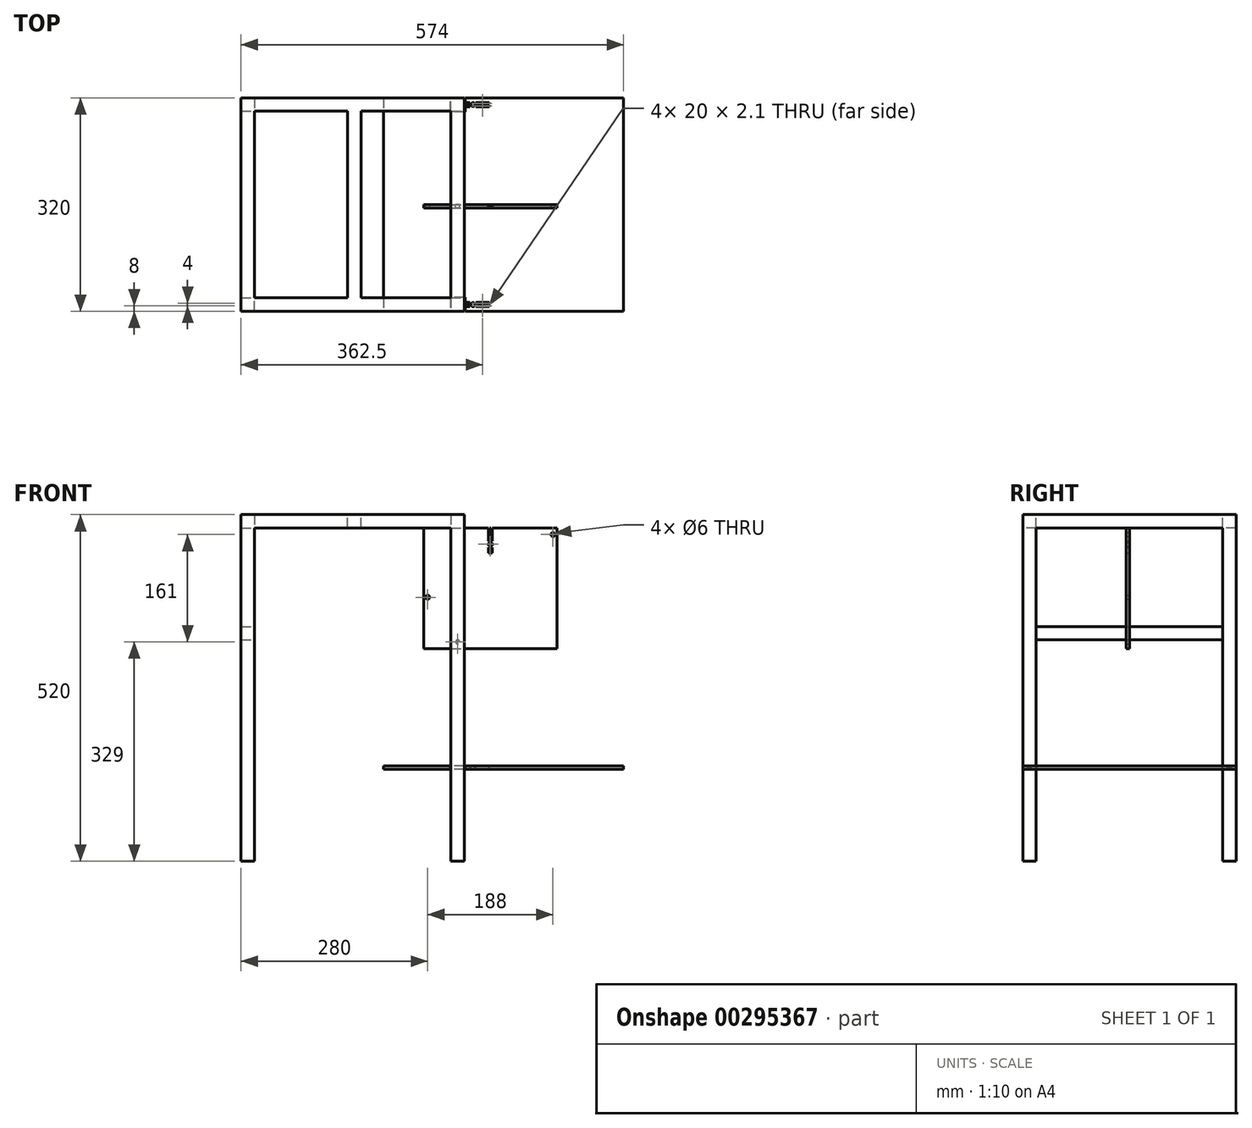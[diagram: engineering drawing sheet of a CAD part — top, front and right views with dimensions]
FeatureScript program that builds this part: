
annotation { "Feature Type Name" : "Feature", "Feature Type Description" : "" }
export const myFeature = defineFeature(function(context is Context, id is Id, definition is map)
    precondition{}
    {
        {
            var Q0;
            Q0=qCreatedBy(makeId("Front.planeOp"),FACE);
            var sketch = newSketch(context, id + "F0", { "sketchPlane" : qUnion([Q0])});
            skCircle(sketch, "E0", {"center": v(0, 0) * mm, "radius": 3 * mm});
            skCircle(sketch, "E1", {"center": v(-45, 67) * mm, "radius": 3 * mm});
            skCircle(sketch, "E2", {"center": v(143, 161) * mm, "radius": 3 * mm});
            skLineSegment(sketch, "E3.bottom", {"start": v(-51, -10) * mm, "end": v(149, -10) * mm});
            skLineSegment(sketch, "E3.top", {"start": v(-51, 171) * mm, "end": v(45.95, 171) * mm});
            skLineSegment(sketch, "E3.left", {"start": v(-51, -10) * mm, "end": v(-51, 171) * mm});
            skLineSegment(sketch, "E3.right", {"start": v(149, -10) * mm, "end": v(149, 171) * mm});
            skCircle(sketch, "E4", {"center": v(49, 146.5) * mm, "radius": 3 * mm});
            skPoint(sketch, "E4.centerSnap0", {"position": v(49, 171) * mm});
            skLineSegment(sketch, "E5.top", {"start": v(45.95, 151) * mm, "end": v(48.05, 151) * mm});
            skLineSegment(sketch, "E5.left", {"start": v(45.95, 171) * mm, "end": v(45.95, 151) * mm});
            skLineSegment(sketch, "E5.right", {"start": v(48.05, 171) * mm, "end": v(48.05, 151) * mm});
            skLineSegment(sketch, "E6.bottom", {"start": v(45.95, 141.5) * mm, "end": v(48.05, 141.5) * mm});
            skLineSegment(sketch, "E6.top", {"start": v(45.95, 133.5) * mm, "end": v(48.05, 133.5) * mm});
            skLineSegment(sketch, "E6.left", {"start": v(45.95, 141.5) * mm, "end": v(45.95, 133.5) * mm});
            skLineSegment(sketch, "E6.right", {"start": v(48.05, 141.5) * mm, "end": v(48.05, 133.5) * mm});
            skLineSegment(sketch, "E7.trimOffspring", {"start": v(48.05, 171) * mm, "end": v(49.95, 171) * mm});
            skLineSegment(sketch, "E8.MirrorCS", {"start": v(52.05, 133.5) * mm, "end": v(49.95, 133.5) * mm});
            skLineSegment(sketch, "E9.MirrorCS", {"start": v(52.05, 141.5) * mm, "end": v(49.95, 141.5) * mm});
            skLineSegment(sketch, "E10.MirrorCS", {"start": v(49.95, 171) * mm, "end": v(49.95, 151) * mm});
            skLineSegment(sketch, "E11.MirrorCS", {"start": v(52.05, 151) * mm, "end": v(49.95, 151) * mm});
            skLineSegment(sketch, "E12.MirrorCS", {"start": v(52.05, 141.5) * mm, "end": v(52.05, 133.5) * mm});
            skLineSegment(sketch, "E13.MirrorCS", {"start": v(49.95, 141.5) * mm, "end": v(49.95, 133.5) * mm});
            skLineSegment(sketch, "E14.MirrorCS", {"start": v(52.05, 171) * mm, "end": v(52.05, 151) * mm});
            skLineSegment(sketch, "E15.trimOffspring", {"start": v(52.05, 171) * mm, "end": v(149, 171) * mm});
            skSolve(sketch);
        }
        {
            var Q0;
            Q0=makeQuery(id+"F0.imprint","IMPRINT",FACE,{"disambiguationData":[TD([[makeQuery(id+"F0.imprint","IMPRINT",EDGE,{"derivedFrom":sQuery(id+"F0.wireOp",EDGE,"E0")}),-1.0]])]});
            extrude(context, id + "F1", {"entities" : qUnion([Q0]), "depth" : 5 * mm});
        }
        {
            var Q0;
            Q0=qCreatedBy(makeId("Top.planeOp"),FACE);
            cPlane(context, id + "F2", {"entities" : qUnion([Q0]), "cplaneType" : CPlaneType.OFFSET, "offset" : 171 * mm, "width" : 150 * mm, "height" : 150 * mm});
        }
        {
            var Q0;
            Q0=qCreatedBy(id+"F2.planeOp",FACE);
            var sketch = newSketch(context, id + "F3", { "sketchPlane" : qUnion([Q0])});
            skLineSegment(sketch, "E16.bottom", {"start": v(10, -160) * mm, "end": v(-10, -160) * mm});
            skLineSegment(sketch, "E16.top", {"start": v(10, 160) * mm, "end": v(-10, 160) * mm});
            skLineSegment(sketch, "E16.left", {"start": v(10, -160) * mm, "end": v(10, 160) * mm});
            skLineSegment(sketch, "E16.right", {"start": v(-10, -160) * mm, "end": v(-10, 160) * mm});
            skLineSegment(sketch, "E17.bottom", {"start": v(-10, 160) * mm, "end": v(-305, 160) * mm});
            skLineSegment(sketch, "E17.top", {"start": v(-10, 140) * mm, "end": v(-305, 140) * mm});
            skLineSegment(sketch, "E17.left", {"start": v(-10, 160) * mm, "end": v(-10, 140) * mm});
            skLineSegment(sketch, "E17.right", {"start": v(-305, 160) * mm, "end": v(-305, 140) * mm});
            skLineSegment(sketch, "E18.bottom", {"start": v(-10, -160) * mm, "end": v(-305, -160) * mm});
            skLineSegment(sketch, "E18.top", {"start": v(-10, -140) * mm, "end": v(-305, -140) * mm});
            skLineSegment(sketch, "E18.left", {"start": v(-10, -160) * mm, "end": v(-10, -140) * mm});
            skLineSegment(sketch, "E18.right", {"start": v(-305, -160) * mm, "end": v(-305, -140) * mm});
            skLineSegment(sketch, "E19.bottom", {"start": v(-305, 160) * mm, "end": v(-325, 160) * mm});
            skLineSegment(sketch, "E19.top", {"start": v(-305, -160) * mm, "end": v(-325, -160) * mm});
            skLineSegment(sketch, "E19.left", {"start": v(-305, 160) * mm, "end": v(-305, -160) * mm});
            skLineSegment(sketch, "E19.right", {"start": v(-325, 160) * mm, "end": v(-325, -160) * mm});
            skSolve(sketch);
        }
        {
            var Q0;
            Q0=qSketchRegion(id+"F3",true);
            extrude(context, id + "F4", {"entities" : qUnion([Q0]), "operationType" : NewBodyOperationType.ADD, "depth" : 20 * mm});
        }
        {
            var Q0;
            Q0=makeQuery(id+"F4.opExtrude","CAP_FACE",FACE,{"disambiguationData":[OSD([sQuery(id+"F3.wireOp",EDGE,"E16.bottom"),sQuery(id+"F3.wireOp",EDGE,"E16.top"),sQuery(id+"F3.wireOp",EDGE,"E16.left"),sQuery(id+"F3.wireOp",EDGE,"E16.right"),sQuery(id+"F3.wireOp",EDGE,"7mnNWSTb-ftgJ-FYnv-rSfW-03W7qfMdHJeY.bottom"),sQuery(id+"F3.wireOp",EDGE,"7mnNWSTb-ftgJ-FYnv-rSfW-03W7qfMdHJeY.top"),sQuery(id+"F3.wireOp",EDGE,"yphk7Mg7-LXwZ-R6qe-Yzbn-fpSbBpRDTs4J.bottom"),sQuery(id+"F3.wireOp",EDGE,"yphk7Mg7-LXwZ-R6qe-Yzbn-fpSbBpRDTs4J.top"),sQuery(id+"F3.wireOp",EDGE,"yphk7Mg7-LXwZ-R6qe-Yzbn-fpSbBpRDTs4J.left"),sQuery(id+"F3.wireOp",EDGE,"yphk7Mg7-LXwZ-R6qe-Yzbn-fpSbBpRDTs4J.right"),sQuery(id+"F3.wireOp",EDGE,"9GNo11h2-buUj-PFzF-0UOW-2sDmyF7RkODV.bottom"),sQuery(id+"F3.wireOp",EDGE,"9GNo11h2-buUj-PFzF-0UOW-2sDmyF7RkODV.top")])],"isStart":true});
            var sketch = newSketch(context, id + "F5", { "sketchPlane" : qUnion([Q0])});
            skLineSegment(sketch, "E20.bottom", {"start": v(-325, 160) * mm, "end": v(-305, 160) * mm});
            skLineSegment(sketch, "E20.top", {"start": v(-325, 140) * mm, "end": v(-305, 140) * mm});
            skLineSegment(sketch, "E20.left", {"start": v(-325, 160) * mm, "end": v(-325, 140) * mm});
            skLineSegment(sketch, "E20.right", {"start": v(-305, 160) * mm, "end": v(-305, 140) * mm});
            skLineSegment(sketch, "E21.bottom", {"start": v(-325, -160) * mm, "end": v(-305, -160) * mm});
            skLineSegment(sketch, "E21.top", {"start": v(-325, -140) * mm, "end": v(-305, -140) * mm});
            skLineSegment(sketch, "E21.left", {"start": v(-325, -160) * mm, "end": v(-325, -140) * mm});
            skLineSegment(sketch, "E21.right", {"start": v(-305, -160) * mm, "end": v(-305, -140) * mm});
            skLineSegment(sketch, "E22.bottom", {"start": v(-10, -140) * mm, "end": v(10, -140) * mm});
            skLineSegment(sketch, "E22.top", {"start": v(-10, -160) * mm, "end": v(10, -160) * mm});
            skLineSegment(sketch, "E22.left", {"start": v(-10, -140) * mm, "end": v(-10, -160) * mm});
            skLineSegment(sketch, "E22.right", {"start": v(10, -140) * mm, "end": v(10, -160) * mm});
            skLineSegment(sketch, "E23.bottom", {"start": v(-10, 140) * mm, "end": v(10, 140) * mm});
            skLineSegment(sketch, "E23.top", {"start": v(-10, 160) * mm, "end": v(10, 160) * mm});
            skLineSegment(sketch, "E23.left", {"start": v(-10, 140) * mm, "end": v(-10, 160) * mm});
            skLineSegment(sketch, "E23.right", {"start": v(10, 140) * mm, "end": v(10, 160) * mm});
            skSolve(sketch);
        }
        {
            var Q0;
            Q0=qSketchRegion(id+"F5",true);
            extrude(context, id + "F6", {"entities" : qUnion([Q0]), "operationType" : NewBodyOperationType.ADD, "depth" : 500 * mm});
        }
        {
            var Q0;
            Q0=qCreatedBy(makeId("Top.planeOp"),FACE);
            cPlane(context, id + "F7", {"entities" : qUnion([Q0]), "cplaneType" : CPlaneType.OFFSET, "offset" : 186 * mm, "oppositeDirection" : true, "width" : 150 * mm, "height" : 150 * mm});
        }
        {
            var Q0;
            Q0=qCreatedBy(id+"F7.planeOp",FACE);
            var sketch = newSketch(context, id + "F8", { "sketchPlane" : qUnion([Q0])});
            skLineSegment(sketch, "E24.bottom", {"start": v(11, -139) * mm, "end": v(-11, -139) * mm});
            skPoint(sketch, "E24.middle", {"position": v(69, 0) * mm});
            skLineSegment(sketch, "E25.top", {"start": v(-111, 160) * mm, "end": v(-11, 160) * mm});
            skLineSegment(sketch, "E26.top", {"start": v(-111, -160) * mm, "end": v(-11, -160) * mm});
            skLineSegment(sketch, "E27.top", {"start": v(249, 160) * mm, "end": v(11, 160) * mm});
            skLineSegment(sketch, "E28.top", {"start": v(249, -160) * mm, "end": v(11, -160) * mm});
            skLineSegment(sketch, "E28.right", {"start": v(11, -139) * mm, "end": v(11, -146.95) * mm});
            skLineSegment(sketch, "E29", {"start": v(11, 160) * mm, "end": v(11, 153.05) * mm});
            skLineSegment(sketch, "E30", {"start": v(11, 139) * mm, "end": v(-11, 139) * mm});
            skLineSegment(sketch, "E31", {"start": v(-11, 139) * mm, "end": v(-11, 160) * mm});
            skCircle(sketch, "E32", {"center": v(23, 150) * mm, "radius": 3 * mm});
            skLineSegment(sketch, "E33.top", {"start": v(27.5, 153.05) * mm, "end": v(27.5, 150.95) * mm});
            skLineSegment(sketch, "E33.left", {"start": v(47.5, 153.05) * mm, "end": v(27.5, 153.05) * mm});
            skLineSegment(sketch, "E33.right", {"start": v(47.5, 150.95) * mm, "end": v(27.5, 150.95) * mm});
            skLineSegment(sketch, "E34.bottom", {"start": v(18, 153.05) * mm, "end": v(18, 150.95) * mm});
            skLineSegment(sketch, "E34.left", {"start": v(18, 153.05) * mm, "end": v(11, 153.05) * mm});
            skLineSegment(sketch, "E34.right", {"start": v(18, 150.95) * mm, "end": v(11, 150.95) * mm});
            skLineSegment(sketch, "E35.MirrorCS", {"start": v(18, 146.95) * mm, "end": v(18, 149.05) * mm});
            skLineSegment(sketch, "E36.MirrorCS", {"start": v(47.5, 149.05) * mm, "end": v(27.5, 149.05) * mm});
            skLineSegment(sketch, "E37.MirrorCS", {"start": v(27.5, 146.95) * mm, "end": v(27.5, 149.05) * mm});
            skLineSegment(sketch, "E38.MirrorCS", {"start": v(18, 146.95) * mm, "end": v(11, 146.95) * mm});
            skLineSegment(sketch, "E39.MirrorCS", {"start": v(18, 149.05) * mm, "end": v(11, 149.05) * mm});
            skLineSegment(sketch, "E40.MirrorCS", {"start": v(47.5, 146.95) * mm, "end": v(27.5, 146.95) * mm});
            skLineSegment(sketch, "E41", {"start": v(47.5, 146.95) * mm, "end": v(47.5, 149.05) * mm});
            skLineSegment(sketch, "E42", {"start": v(47.5, 150.95) * mm, "end": v(47.5, 153.05) * mm});
            skLineSegment(sketch, "E43.trimOffspring", {"start": v(11, 150.95) * mm, "end": v(11, 149.05) * mm});
            skLineSegment(sketch, "E44.trimOffspring", {"start": v(11, 146.95) * mm, "end": v(11, 139) * mm});
            skLineSegment(sketch, "E45", {"start": v(-11, -139) * mm, "end": v(-11, -160) * mm});
            skLineSegment(sketch, "E46", {"start": v(-111, 160) * mm, "end": v(-111, -160) * mm});
            skLineSegment(sketch, "E47", {"start": v(249, 160) * mm, "end": v(249, -160) * mm});
            skCircle(sketch, "E48", {"center": v(23, -150) * mm, "radius": 3 * mm});
            skLineSegment(sketch, "E49.top", {"start": v(27.5, -146.95) * mm, "end": v(27.5, -149.05) * mm});
            skLineSegment(sketch, "E49.left", {"start": v(47.5, -146.95) * mm, "end": v(27.5, -146.95) * mm});
            skLineSegment(sketch, "E49.right", {"start": v(47.5, -149.05) * mm, "end": v(27.5, -149.05) * mm});
            skLineSegment(sketch, "E50.bottom", {"start": v(18, -146.95) * mm, "end": v(18, -149.05) * mm});
            skLineSegment(sketch, "E50.left", {"start": v(18, -146.95) * mm, "end": v(11, -146.95) * mm});
            skLineSegment(sketch, "E50.right", {"start": v(18, -149.05) * mm, "end": v(11, -149.05) * mm});
            skLineSegment(sketch, "E51.MirrorCS", {"start": v(18, -153.05) * mm, "end": v(18, -150.95) * mm});
            skLineSegment(sketch, "E52.MirrorCS", {"start": v(47.5, -150.95) * mm, "end": v(27.5, -150.95) * mm});
            skLineSegment(sketch, "E53.MirrorCS", {"start": v(27.5, -153.05) * mm, "end": v(27.5, -150.95) * mm});
            skLineSegment(sketch, "E54.MirrorCS", {"start": v(18, -153.05) * mm, "end": v(11, -153.05) * mm});
            skLineSegment(sketch, "E55.MirrorCS", {"start": v(18, -150.95) * mm, "end": v(11, -150.95) * mm});
            skLineSegment(sketch, "E56.MirrorCS", {"start": v(47.5, -153.05) * mm, "end": v(27.5, -153.05) * mm});
            skLineSegment(sketch, "E57", {"start": v(47.5, -153.05) * mm, "end": v(47.5, -150.95) * mm});
            skLineSegment(sketch, "E58", {"start": v(47.5, -149.05) * mm, "end": v(47.5, -146.95) * mm});
            skLineSegment(sketch, "E59.trimOffspring", {"start": v(11, -149.05) * mm, "end": v(11, -150.95) * mm});
            skLineSegment(sketch, "E60.trimOffspring", {"start": v(11, -153.05) * mm, "end": v(11, -160) * mm});
            skLineSegment(sketch, "E61", {"start": v(0, 0) * mm, "end": v(0, 174.93) * mm});
            skSolve(sketch);
        }
        {
            var Q0;
            Q0=makeQuery(id+"F8.imprint","IMPRINT",FACE,{"disambiguationData":[TD([[makeQuery(id+"F8.imprint","IMPRINT",EDGE,{"derivedFrom":sQuery(id+"F8.wireOp",EDGE,"E24.bottom")}),-1.0]])]});
            extrude(context, id + "F9", {"entities" : qUnion([Q0]), "operationType" : NewBodyOperationType.ADD, "oppositeDirection" : true, "depth" : 5 * mm});
        }
        {
            var Q0;
            Q0=makeQuery(id+"F6.opExtrude","SWEPT_FACE",FACE,{"disambiguationData":[OSD([sQuery(id+"F5.wireOp",EDGE,"E21.top")])]});
            var sketch = newSketch(context, id + "F10", { "sketchPlane" : qUnion([Q0])});
            skLineSegment(sketch, "E62.bottom", {"start": v(-325, 3) * mm, "end": v(-305, 3) * mm});
            skLineSegment(sketch, "E62.top", {"start": v(-325, 23) * mm, "end": v(-305, 23) * mm});
            skLineSegment(sketch, "E62.left", {"start": v(-325, 3) * mm, "end": v(-325, 23) * mm});
            skLineSegment(sketch, "E62.right", {"start": v(-305, 3) * mm, "end": v(-305, 23) * mm});
            skSolve(sketch);
        }
        {
            var Q0;
            Q0=qSketchRegion(id+"F10",true);
            extrude(context, id + "F11", {"entities" : qUnion([Q0]), "operationType" : NewBodyOperationType.ADD, "depth" : 280 * mm});
        }
        {
            var Q0;
            Q0=makeQuery(id+"F4.opExtrude","SWEPT_FACE",FACE,{"disambiguationData":[OSD([sQuery(id+"F3.wireOp",EDGE,"E17.top")])]});
            var sketch = newSketch(context, id + "F12", { "sketchPlane" : qUnion([Q0])});
            skLineSegment(sketch, "E63.bottom", {"start": v(-165, 171) * mm, "end": v(-145, 171) * mm});
            skLineSegment(sketch, "E63.top", {"start": v(-165, 191) * mm, "end": v(-145, 191) * mm});
            skLineSegment(sketch, "E63.left", {"start": v(-165, 171) * mm, "end": v(-165, 191) * mm});
            skLineSegment(sketch, "E63.right", {"start": v(-145, 171) * mm, "end": v(-145, 191) * mm});
            skSolve(sketch);
        }
        {
            var Q0;
            Q0=makeQuery(id+"F12.imprint","IMPRINT",FACE,{"disambiguationData":[TD([[makeQuery(id+"F12.imprint","IMPRINT",EDGE,{"derivedFrom":sQuery(id+"F12.wireOp",EDGE,"E63.bottom")}),-1.0]])]});
            extrude(context, id + "F13", {"entities" : qUnion([Q0]), "operationType" : NewBodyOperationType.ADD, "depth" : 280 * mm});
        }
    });
